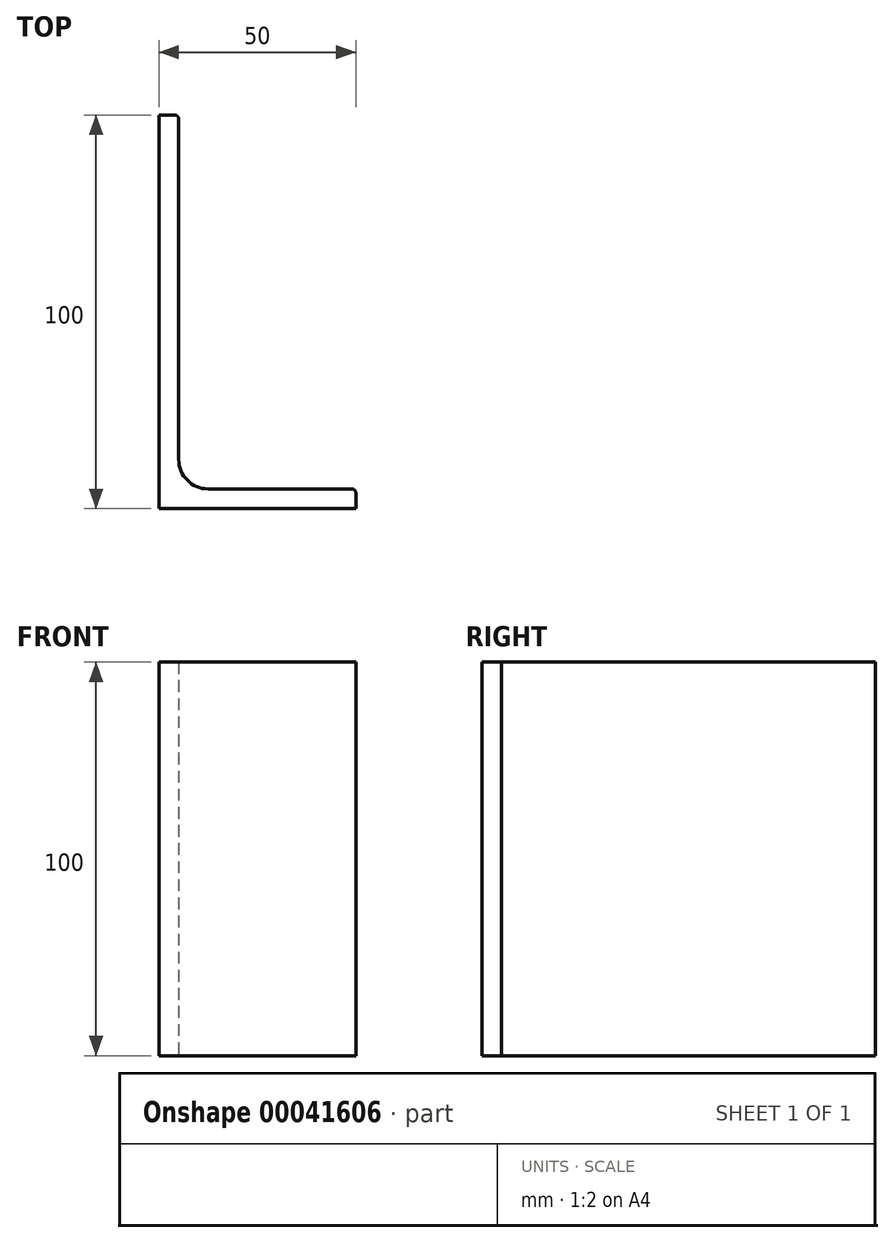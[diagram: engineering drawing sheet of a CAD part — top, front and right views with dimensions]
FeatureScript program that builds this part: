
annotation { "Feature Type Name" : "Feature", "Feature Type Description" : "" }
export const myFeature = defineFeature(function(context is Context, id is Id, definition is map)
    precondition{}
    {
        {
            var Q0;
            Q0=qCreatedBy(makeId("Top.planeOp"),FACE);
            var sketch = newSketch(context, id + "F0", { "sketchPlane" : qUnion([Q0])});
            skLineSegment(sketch, "E0.rect.top", {"start": v(-25, -50) * mm, "end": v(25, -50) * mm});
            skLineSegment(sketch, "E0.rect.left", {"start": v(-25, 50) * mm, "end": v(-25, -50) * mm});
            skPoint(sketch, "E0.rect.middle", {"position": v(0, 0) * mm});
            skLineSegment(sketch, "E1.0", {"start": v(-12.5, -45) * mm, "end": v(25, -45) * mm});
            skLineSegment(sketch, "E1.1", {"start": v(-20, 50) * mm, "end": v(-20, -37.5) * mm});
            skLineSegment(sketch, "E2", {"start": v(25, -45) * mm, "end": v(25, -50) * mm});
            skLineSegment(sketch, "E3", {"start": v(-25, 50) * mm, "end": v(-20, 50) * mm});
            skPoint(sketch, "E4.visualSharp", {"position": v(-20, -45) * mm});
            skArc(sketch, "E4.filletArc", {"start": v(-20, -37.5) * mm, "mid": v(-17.8, -42.8) * mm, "end": v(-12.5, -45) * mm});
            skSolve(sketch);
        }
        {
            var Q0;
            Q0=makeQuery(id+"F0.imprint","IMPRINT",FACE,{"disambiguationData":[TD([[makeQuery(id+"F0.imprint","IMPRINT",EDGE,{"derivedFrom":sQuery(id+"F0.wireOp",EDGE,"E0.rect.bottom")}),-1.0]])]});
            var Q1;
            Q1=makeQuery(id+"F0.imprint","IMPRINT",FACE,{"disambiguationData":[TD([[makeQuery(id+"F0.imprint","IMPRINT",EDGE,{"derivedFrom":sQuery(id+"F0.wireOp",EDGE,"E0.rect.top")}),1.0]])]});
            extrude(context, id + "F1", {"entities" : qUnion([Q0, Q1]), "depth" : 100 * mm});
        }
        {
            var Q0;
            Q0=makeQuery(id+"F1.opExtrude","SWEPT_EDGE",EDGE,{"disambiguationData":[OSD([sQuery(id+"F0.wireOp",EDGE,"E1.1"),sQuery(id+"F0.wireOp",EDGE,"E3")])]});
            var Q1;
            Q1=makeQuery(id+"F1.opExtrude","SWEPT_EDGE",EDGE,{"disambiguationData":[OSD([sQuery(id+"F0.wireOp",EDGE,"E1.0"),sQuery(id+"F0.wireOp",EDGE,"E2")])]});
            fillet(context, id + "F2", {"entities" : qUnion([Q0, Q1]), "radius" : 1 * mm, "tangentPropagation" : true, "allowEdgeOverflow" : false});
        }
    });
